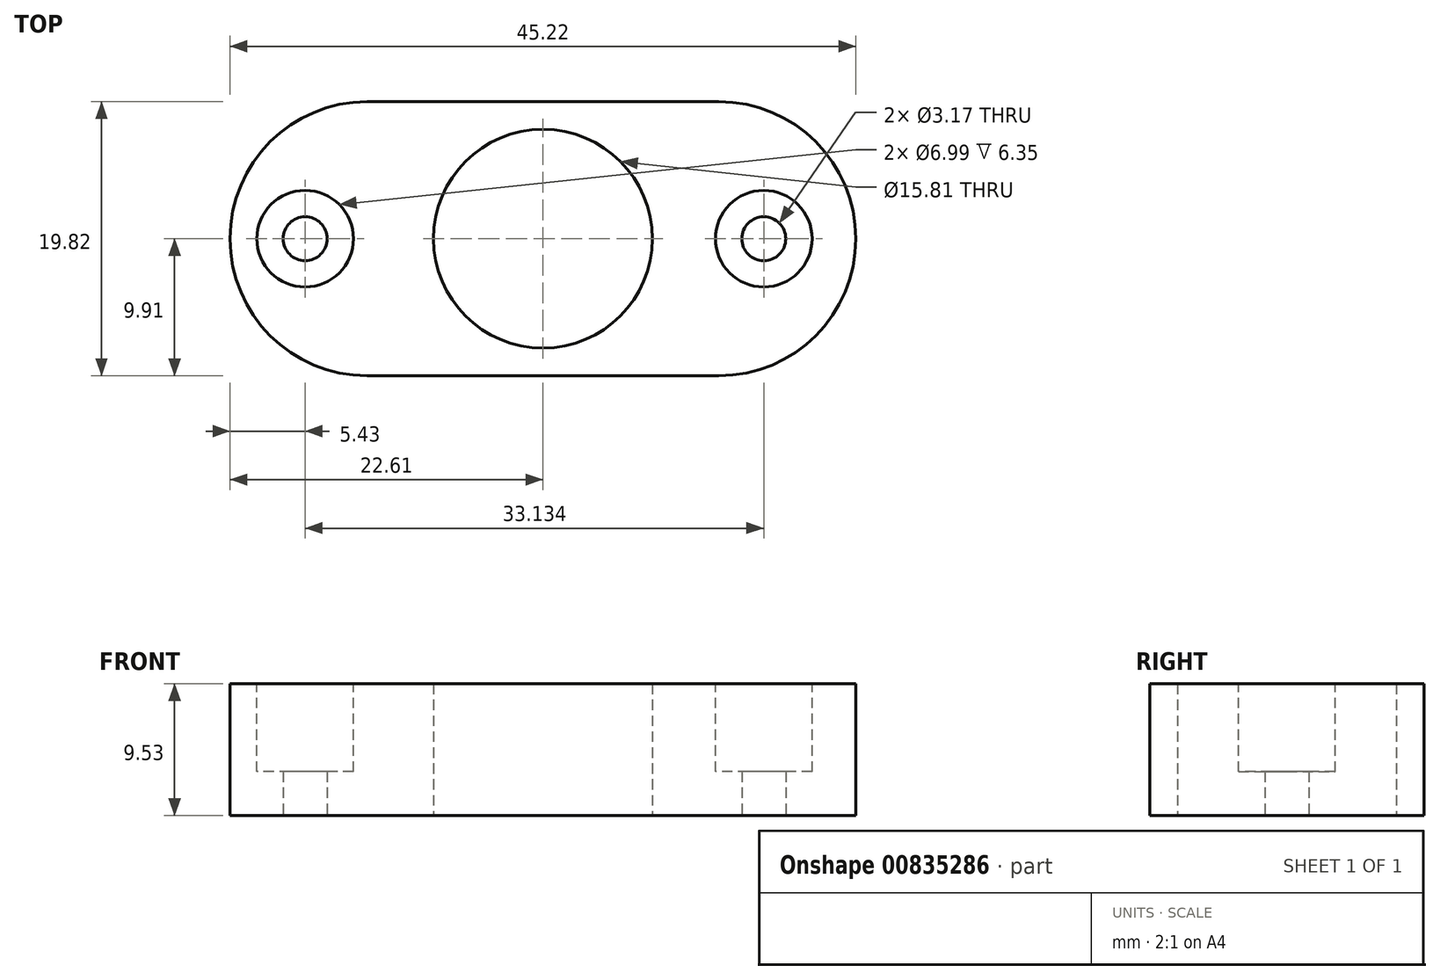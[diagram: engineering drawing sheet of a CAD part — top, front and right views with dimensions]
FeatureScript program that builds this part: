
annotation { "Feature Type Name" : "Feature", "Feature Type Description" : "" }
export const myFeature = defineFeature(function(context is Context, id is Id, definition is map)
    precondition{}
    {
        {
            var Q0;
            Q0=qCreatedBy(makeId("Top.planeOp"),FACE);
            var sketch = newSketch(context, id + "F0", { "sketchPlane" : qUnion([Q0])});
            skLineSegment(sketch, "E0", {"start": v(0, 25.4) * mm, "end": v(25.4, 0) * mm, "construction": true});
            skLineSegment(sketch, "E1", {"start": v(0, 0) * mm, "end": v(25.4, 25.4) * mm, "construction": true});
            skCircle(sketch, "E2", {"center": v(12.7, 12.7) * mm, "radius": 7.14 * mm});
            skLineSegment(sketch, "E3", {"start": v(12.7, 12.7) * mm, "end": v(47.78, 12.7) * mm, "construction": true});
            skLineSegment(sketch, "E4", {"start": v(12.7, 12.7) * mm, "end": v(-24.84, 12.7) * mm, "construction": true});
            skCircle(sketch, "E5", {"center": v(-4.48, 12.7) * mm, "radius": 1.59 * mm});
            skCircle(sketch, "E6", {"center": v(28.65, 12.7) * mm, "radius": 1.59 * mm});
            skLineSegment(sketch, "E7.0", {"start": v(0, 22.6) * mm, "end": v(25.4, 22.6) * mm});
            skArc(sketch, "E7.1", {"start": v(0, 22.6) * mm, "mid": v(-9.9, 12.7) * mm, "end": v(0, 2.8) * mm});
            skLineSegment(sketch, "E7.2", {"start": v(0, 2.8) * mm, "end": v(25.4, 2.8) * mm});
            skArc(sketch, "E7.3", {"start": v(25.4, 2.8) * mm, "mid": v(35.3, 12.7) * mm, "end": v(25.4, 22.6) * mm});
            skCircle(sketch, "E8.0", {"center": v(12.7, 12.7) * mm, "radius": 7.9 * mm});
            skSolve(sketch);
        }
        {
            var Q0;
            Q0 = qSketchRegion(id + "F0", true);
            extrude(context, id + "F1", {"entities" : qUnion([Q0]), "depth" : 9.52 * mm, "offsetDistance" : 25.4 * mm});
        }
        {
            var Q0;
            Q0=makeQuery(id+"F1.opExtrude","CAP_FACE",FACE,{"disambiguationData":[OSD([sQuery(id+"F0.wireOp",EDGE,"E5"),sQuery(id+"F0.wireOp",EDGE,"E6"),sQuery(id+"F0.wireOp",EDGE,"E7.0"),sQuery(id+"F0.wireOp",EDGE,"E7.1"),sQuery(id+"F0.wireOp",EDGE,"E7.2"),sQuery(id+"F0.wireOp",EDGE,"E7.3"),sQuery(id+"F0.wireOp",EDGE,"E8.0")])],"isStart":false});
            var sketch = newSketch(context, id + "F2", { "sketchPlane" : qUnion([Q0])});
            skCircle(sketch, "E9", {"center": v(-4.48, 12.7) * mm, "radius": 3.5 * mm});
            skCircle(sketch, "E10", {"center": v(28.65, 12.7) * mm, "radius": 3.5 * mm});
            skSolve(sketch);
        }
        {
            var Q0;
            Q0=makeQuery(id+"F2.imprint","IMPRINT",FACE,{"disambiguationData":[TD([[makeQuery(id+"F2.imprint","IMPRINT",EDGE,{"derivedFrom":sQuery(id+"F2.wireOp",EDGE,"E9")}),1.0]])]});
            var Q1;
            Q1=makeQuery(id+"F2.imprint","IMPRINT",FACE,{"disambiguationData":[TD([[makeQuery(id+"F2.imprint","IMPRINT",EDGE,{"derivedFrom":sQuery(id+"F2.wireOp",EDGE,"E10")}),1.0]])]});
            extrude(context, id + "F3", {"entities" : qUnion([Q0, Q1]), "operationType" : NewBodyOperationType.REMOVE, "oppositeDirection" : true, "depth" : 6.35 * mm, "offsetDistance" : 25.4 * mm});
        }
    });
